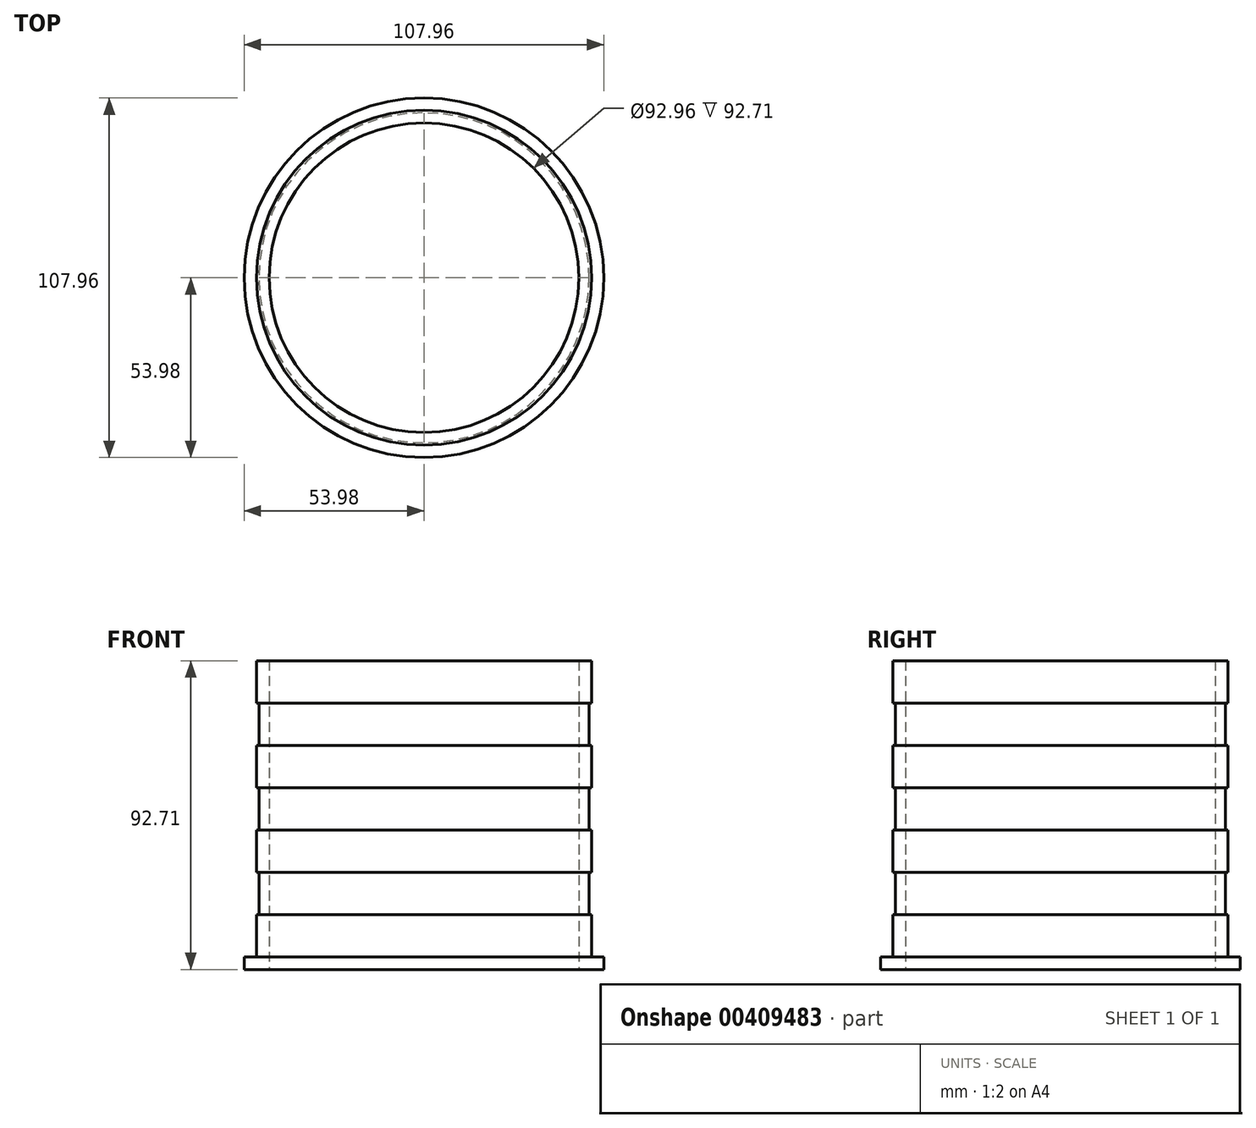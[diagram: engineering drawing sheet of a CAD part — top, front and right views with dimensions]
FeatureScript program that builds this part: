
annotation { "Feature Type Name" : "Feature", "Feature Type Description" : "" }
export const myFeature = defineFeature(function(context is Context, id is Id, definition is map)
    precondition{}
    {
        {
            var Q0;
            Q0=qCreatedBy(makeId("Front.planeOp"),FACE);
            var sketch = newSketch(context, id + "F0", { "sketchPlane" : qUnion([Q0])});
            skLineSegment(sketch, "E0", {"start": v(-53.98, -54.61) * mm, "end": v(-53.98, -50.8) * mm});
            skLineSegment(sketch, "E1", {"start": v(-53.98, -50.8) * mm, "end": v(-50.3, -50.8) * mm});
            skLineSegment(sketch, "E2", {"start": v(-50.3, -50.8) * mm, "end": v(-50.3, -38.1) * mm});
            skLineSegment(sketch, "E3", {"start": v(-50.3, -38.1) * mm, "end": v(-49.53, -38.1) * mm});
            skLineSegment(sketch, "E4", {"start": v(-49.53, -38.1) * mm, "end": v(-49.53, -25.4) * mm});
            skLineSegment(sketch, "E5", {"start": v(-49.53, -25.4) * mm, "end": v(-50.3, -25.4) * mm});
            skLineSegment(sketch, "E6", {"start": v(-50.3, -25.4) * mm, "end": v(-50.3, -12.7) * mm});
            skLineSegment(sketch, "E7", {"start": v(-50.3, -12.7) * mm, "end": v(-49.53, -12.7) * mm});
            skLineSegment(sketch, "E8", {"start": v(-49.53, -12.7) * mm, "end": v(-49.53, 0) * mm});
            skLineSegment(sketch, "E9", {"start": v(-49.53, 0) * mm, "end": v(-50.3, 0) * mm});
            skLineSegment(sketch, "E10", {"start": v(-50.3, 0) * mm, "end": v(-50.3, 12.7) * mm});
            skLineSegment(sketch, "E11", {"start": v(-50.3, 12.7) * mm, "end": v(-49.53, 12.7) * mm});
            skLineSegment(sketch, "E12", {"start": v(-49.53, 12.7) * mm, "end": v(-49.53, 25.4) * mm});
            skLineSegment(sketch, "E13", {"start": v(-49.53, 25.4) * mm, "end": v(-50.3, 25.4) * mm});
            skLineSegment(sketch, "E14", {"start": v(-50.3, 25.4) * mm, "end": v(-50.3, 38.1) * mm});
            skLineSegment(sketch, "E15", {"start": v(-50.3, 38.1) * mm, "end": v(-49.53, 38.1) * mm});
            skLineSegment(sketch, "E16", {"start": v(-49.53, 38.1) * mm, "end": v(-46.48, 38.1) * mm});
            skLineSegment(sketch, "E17", {"start": v(-46.48, 38.1) * mm, "end": v(-46.48, -54.61) * mm});
            skLineSegment(sketch, "E18", {"start": v(-53.98, -54.61) * mm, "end": v(-46.48, -54.61) * mm});
            skLineSegment(sketch, "E19", {"start": v(0, 0) * mm, "end": v(0, 40.28) * mm});
            skSolve(sketch);
        }
        {
            var Q0;
            Q0=makeQuery(id+"F0.imprint","IMPRINT",FACE,{"disambiguationData":[TD([[makeQuery(id+"F0.imprint","IMPRINT",EDGE,{"derivedFrom":sQuery(id+"F0.wireOp",EDGE,"E0")}),-1.0]])]});
            var Q1;
            Q1=sQuery(id+"F0.wireOp",EDGE,"E19");
            revolve(context, id + "F1", {"entities" : qUnion([Q0]), "axis" : qUnion([Q1]), "revolveType" : RevolveType.FULL});
        }
    });
